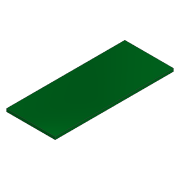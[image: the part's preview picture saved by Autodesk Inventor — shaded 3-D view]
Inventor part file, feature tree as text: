
AUTODESK INVENTOR PART (.ipt)
format: ipt  version: 2020.3 (Build 243373010, 373A)  size: 89,600 bytes
history: native  units: mm
features: extrude x1, sketch x1
ambient origin geometry x8: Origin, YZ Plane, XZ Plane, XY Plane, X Axis, Y Axis, Z Axis, Center Point
bodies: Solid1 (feature_tree)
feature tree (2):
  extrude  "Extrusion1"  Depth=85.0mm
  sketch  "Sketch1"  dims[d0=35.0mm d1=85.0mm d2=2.0mm d3=0.0mm]
